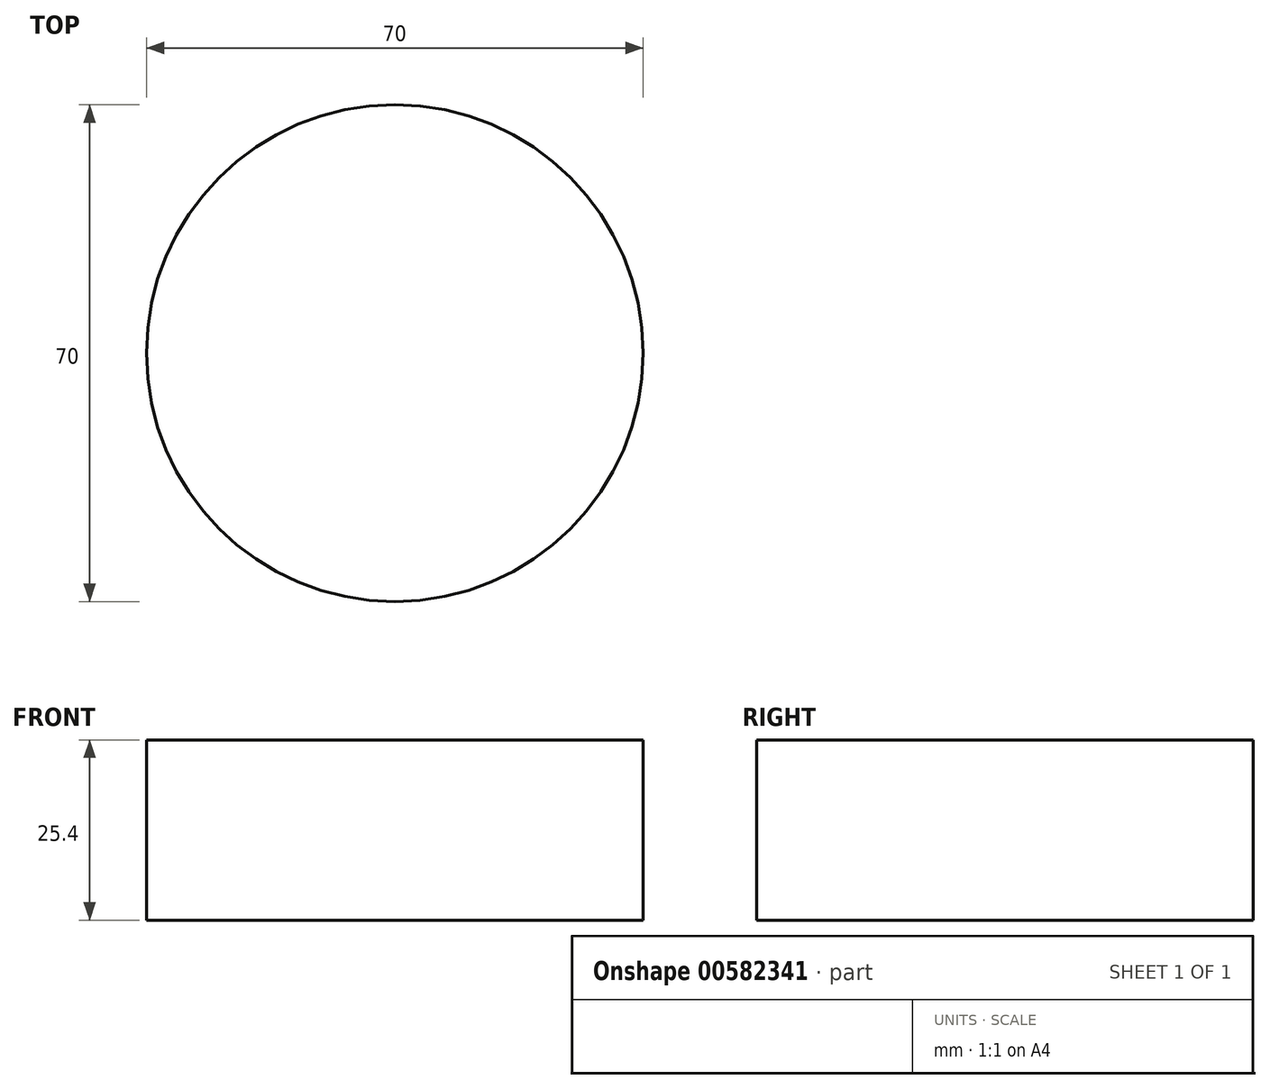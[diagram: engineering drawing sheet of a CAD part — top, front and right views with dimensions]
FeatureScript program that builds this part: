
annotation { "Feature Type Name" : "Feature", "Feature Type Description" : "" }
export const myFeature = defineFeature(function(context is Context, id is Id, definition is map)
    precondition{}
    {
        {
            var Q0;
            Q0=qCreatedBy(makeId("Top.planeOp"),FACE);
            var sketch = newSketch(context, id + "F0", { "sketchPlane" : qUnion([Q0])});
            skCircle(sketch, "E0", {"center": v(0, 0) * mm, "radius": 35 * mm});
            skSolve(sketch);
        }
        {
            var Q0;
            Q0=sQuery(id+"F0.wireOp",EDGE,"E0");
            extrude(context, id + "F1", {"bodyType" : ToolBodyType.SURFACE, "surfaceEntities" : qUnion([Q0]), "depth" : 25.4 * mm, "offsetDistance" : 25.4 * mm});
        }
    });
